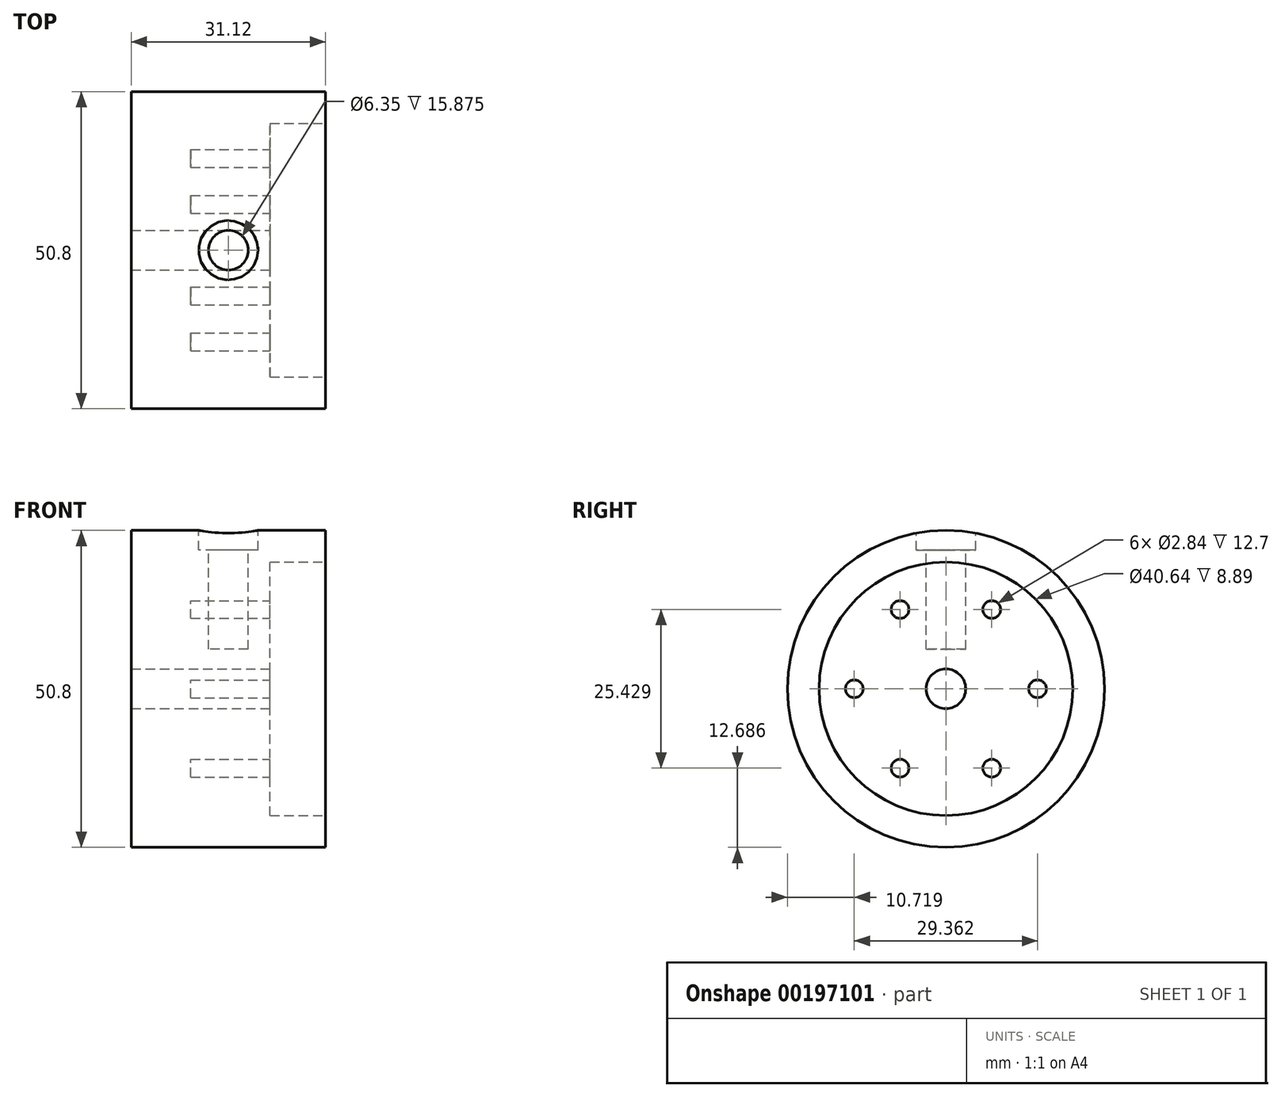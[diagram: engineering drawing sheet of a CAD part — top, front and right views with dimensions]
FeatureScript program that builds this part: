
annotation { "Feature Type Name" : "Feature", "Feature Type Description" : "" }
export const myFeature = defineFeature(function(context is Context, id is Id, definition is map)
    precondition{}
    {
        {
            var Q0;
            Q0=qCreatedBy(makeId("Right.planeOp"),FACE);
            var sketch = newSketch(context, id + "F0", { "sketchPlane" : qUnion([Q0])});
            skCircle(sketch, "E0", {"center": v(0, 0) * mm, "radius": 25.4 * mm});
            skSolve(sketch);
        }
        {
            var Q0;
            Q0 = qSketchRegion(id + "F0", true);
            extrude(context, id + "F1", {"entities" : qUnion([Q0]), "endBound" : BoundingType.SYMMETRIC, "depth" : 31.12 * mm});
        }
        {
            var Q0;
            Q0=makeQuery(id+"F1.opExtrude","CAP_FACE",FACE,{"disambiguationData":[OSD([sQuery(id+"F0.wireOp",EDGE,"E0")])],"isStart":false});
            var sketch = newSketch(context, id + "F2", { "sketchPlane" : qUnion([Q0])});
            skCircle(sketch, "E1", {"center": v(0, 0) * mm, "radius": 3.18 * mm});
            skSolve(sketch);
        }
        {
            var Q0;
            Q0 = qSketchRegion(id + "F2", true);
            extrude(context, id + "F3", {"entities" : qUnion([Q0]), "operationType" : NewBodyOperationType.REMOVE, "endBound" : BoundingType.THROUGH_ALL, "oppositeDirection" : true, "depth" : 25.4 * mm});
        }
        {
            var Q0;
            Q0=makeQuery(id+"F1.opExtrude","CAP_FACE",FACE,{"disambiguationData":[OSD([sQuery(id+"F0.wireOp",EDGE,"E0")])],"isStart":false});
            var sketch = newSketch(context, id + "F4", { "sketchPlane" : qUnion([Q0])});
            skCircle(sketch, "E2", {"center": v(0, 0) * mm, "radius": 20.32 * mm});
            skSolve(sketch);
        }
        {
            var Q0;
            Q0 = qSketchRegion(id + "F4", true);
            extrude(context, id + "F5", {"entities" : qUnion([Q0]), "operationType" : NewBodyOperationType.REMOVE, "oppositeDirection" : true, "depth" : 8.9 * mm});
        }
        {
            var Q0;
            Q0=makeQuery(id+"F5.boolean.opBoolean","COPY",FACE,{"derivedFrom":makeQuery(id+"F5.opExtrude","CAP_FACE",FACE,{"disambiguationData":[OSD([sQuery(id+"F4.wireOp",EDGE,"E2")])],"isStart":false})});
            var sketch = newSketch(context, id + "F6", { "sketchPlane" : qUnion([Q0])});
            skCircle(sketch, "E3", {"center": v(14.68, 0) * mm, "radius": 1.42 * mm});
            skCircle(sketch, "E4.1.0", {"center": v(7.34, -12.71) * mm, "radius": 1.42 * mm});
            skCircle(sketch, "E4.2.0", {"center": v(-7.34, -12.71) * mm, "radius": 1.42 * mm});
            skCircle(sketch, "E4.3.0", {"center": v(-14.68, 0) * mm, "radius": 1.42 * mm});
            skCircle(sketch, "E4.4.0", {"center": v(-7.34, 12.71) * mm, "radius": 1.42 * mm});
            skCircle(sketch, "E4.5.0", {"center": v(7.34, 12.71) * mm, "radius": 1.42 * mm});
            skPoint(sketch, "E4.center", {"position": v(0, 0) * mm});
            skLineSegment(sketch, "E4.anchor1", {"start": v(0, 0) * mm, "end": v(14.68, 0) * mm, "construction": true});
            skLineSegment(sketch, "E4.anchor2", {"start": v(0, 0) * mm, "end": v(7.34, 12.71) * mm, "construction": true});
            skSolve(sketch);
        }
        {
            var Q0;
            Q0 = qSketchRegion(id + "F6", true);
            extrude(context, id + "F7", {"entities" : qUnion([Q0]), "operationType" : NewBodyOperationType.REMOVE, "oppositeDirection" : true, "depth" : 12.7 * mm});
        }
        {
            var Q0;
            Q0=qCreatedBy(makeId("Top.planeOp"),FACE);
            cPlane(context, id + "F8", {"entities" : qUnion([Q0]), "cplaneType" : CPlaneType.OFFSET, "offset" : 25.4 * mm, "width" : 152.4 * mm, "height" : 152.4 * mm});
        }
        {
            var Q0;
            Q0=qCreatedBy(id+"F8.planeOp",FACE);
            var sketch = newSketch(context, id + "F9", { "sketchPlane" : qUnion([Q0])});
            skCircle(sketch, "E5", {"center": v(0, 0) * mm, "radius": 3.18 * mm});
            skCircle(sketch, "E6", {"center": v(0, 0) * mm, "radius": 4.76 * mm});
            skSolve(sketch);
        }
        {
            var Q0;
            Q0 = qSketchRegion(id + "F9", true);
            var Q1;
            Q1=makeQuery(id+"F9.imprint","IMPRINT",FACE,{"disambiguationData":[TD([[makeQuery(id+"F9.imprint","IMPRINT",EDGE,{"derivedFrom":sQuery(id+"F9.wireOp",EDGE,"E5")}),1.0]])]});
            extrude(context, id + "F10", {"entities" : qUnion([Q0, Q1]), "operationType" : NewBodyOperationType.REMOVE, "oppositeDirection" : true, "depth" : 3.17 * mm});
        }
        {
            var Q0;
            Q0=makeQuery(id+"F10.boolean.opBoolean","COPY",FACE,{"derivedFrom":makeQuery(id+"F10.opExtrude","CAP_FACE",FACE,{"disambiguationData":[OSD([sQuery(id+"F9.wireOp",EDGE,"E6")])],"isStart":false})});
            var sketch = newSketch(context, id + "F11", { "sketchPlane" : qUnion([Q0])});
            skCircle(sketch, "E7", {"center": v(0, 0) * mm, "radius": 3.18 * mm});
            skSolve(sketch);
        }
        {
            var Q0;
            Q0 = qSketchRegion(id + "F11", true);
            extrude(context, id + "F12", {"entities" : qUnion([Q0]), "operationType" : NewBodyOperationType.REMOVE, "oppositeDirection" : true, "depth" : 15.88 * mm});
        }
    });
